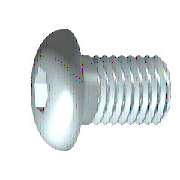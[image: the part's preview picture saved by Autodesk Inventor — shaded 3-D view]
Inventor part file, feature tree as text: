
AUTODESK INVENTOR PART (.ipt)
format: ipt  version: 2015 (Build 190159000, 159)  size: 198,656 bytes
history: native  units: mm (DEFAULTED — no unit token found)
features: sketch x2, extrude x1, plane x1, fillet x1
ambient origin geometry x7: Origin, YZ Plane, XY Plane, X Axis, Y Axis, Z Axis, Center Point
bodies: Solid1 (feature_tree), Body (feature_tree)
feature tree (5):
  extrude  "Slot"  Depth=1.8542mm
  plane  "Work Plane1"
  fillet  "Fillet2"  Radius=1.8542mm
  sketch  "Sketch1"  dims[d1=6.34726mm d2=1.59014mm d3=1.8542mm]
  sketch  "Sketch2"  dims[d4=1.1176mm d5=60.0deg d6=3.5052mm d7=3.5052mm d8=2.287693mm d9=6.6548mm d10=90.0deg d11=10.0mm d12=0.0mm d13=6.34726mm d14=0.0mm d15=0.486918mm d16=0.486918mm d17=1.6002mm d19=0.0mm d26=7.9375mm d27=45.0deg d28=0.0mm d29=0.0mm d30=0.1mm]
